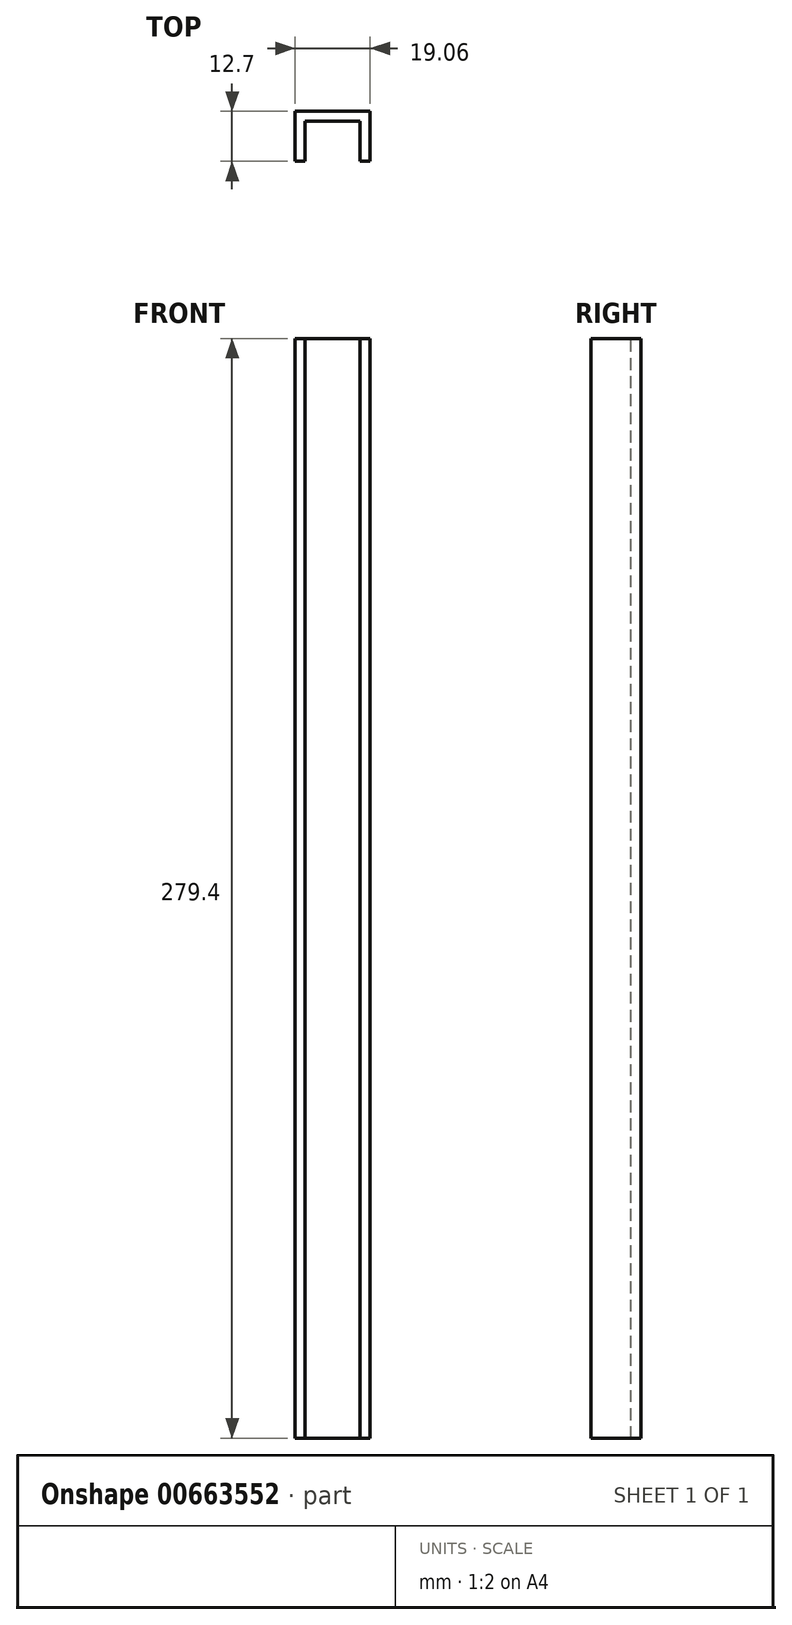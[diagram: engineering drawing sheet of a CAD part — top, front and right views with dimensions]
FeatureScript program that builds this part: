
annotation { "Feature Type Name" : "Feature", "Feature Type Description" : "" }
export const myFeature = defineFeature(function(context is Context, id is Id, definition is map)
    precondition{}
    {
        {
            var Q0;
            Q0=qCreatedBy(makeId("Front.planeOp"),FACE);
            var sketch = newSketch(context, id + "F0", { "sketchPlane" : qUnion([Q0])});
            skLineSegment(sketch, "E0.bottom", {"start": v(-9.52, -139.7) * mm, "end": v(9.53, -139.7) * mm});
            skLineSegment(sketch, "E0.top", {"start": v(-9.53, 139.7) * mm, "end": v(9.52, 139.7) * mm});
            skLineSegment(sketch, "E0.left", {"start": v(-9.52, -139.7) * mm, "end": v(-9.53, 139.7) * mm});
            skLineSegment(sketch, "E0.right", {"start": v(9.53, -139.7) * mm, "end": v(9.52, 139.7) * mm});
            skPoint(sketch, "E0.middle", {"position": v(0, 0) * mm});
            skSolve(sketch);
        }
        {
            var Q0;
            Q0=makeQuery(id+"F0.imprint","IMPRINT",FACE,{"disambiguationData":[TD([[makeQuery(id+"F0.imprint","IMPRINT",EDGE,{"derivedFrom":sQuery(id+"F0.wireOp",EDGE,"E0.bottom")}),1.0]])]});
            extrude(context, id + "F1", {"entities" : qUnion([Q0]), "depth" : 12.7 * mm, "offsetDistance" : 25.4 * mm});
        }
        {
            var Q0;
            Q0=makeQuery(id+"F1.opExtrude","SWEPT_FACE",FACE,{"disambiguationData":[OSD([sQuery(id+"F0.wireOp",EDGE,"E0.top")])]});
            var Q1;
            Q1=makeQuery(id+"F1.opExtrude","CAP_FACE",FACE,{"disambiguationData":[OSD([sQuery(id+"F0.wireOp",EDGE,"E0.bottom"),sQuery(id+"F0.wireOp",EDGE,"E0.top"),sQuery(id+"F0.wireOp",EDGE,"E0.left"),sQuery(id+"F0.wireOp",EDGE,"E0.right")])],"isStart":false});
            var Q2;
            Q2=makeQuery(id+"F1.opExtrude","SWEPT_FACE",FACE,{"disambiguationData":[OSD([sQuery(id+"F0.wireOp",EDGE,"E0.bottom")])]});
            shell(context, id + "F2", {"entities" : qUnion([Q0, Q1, Q2]), "thickness" : 2.54 * mm});
        }
    });
